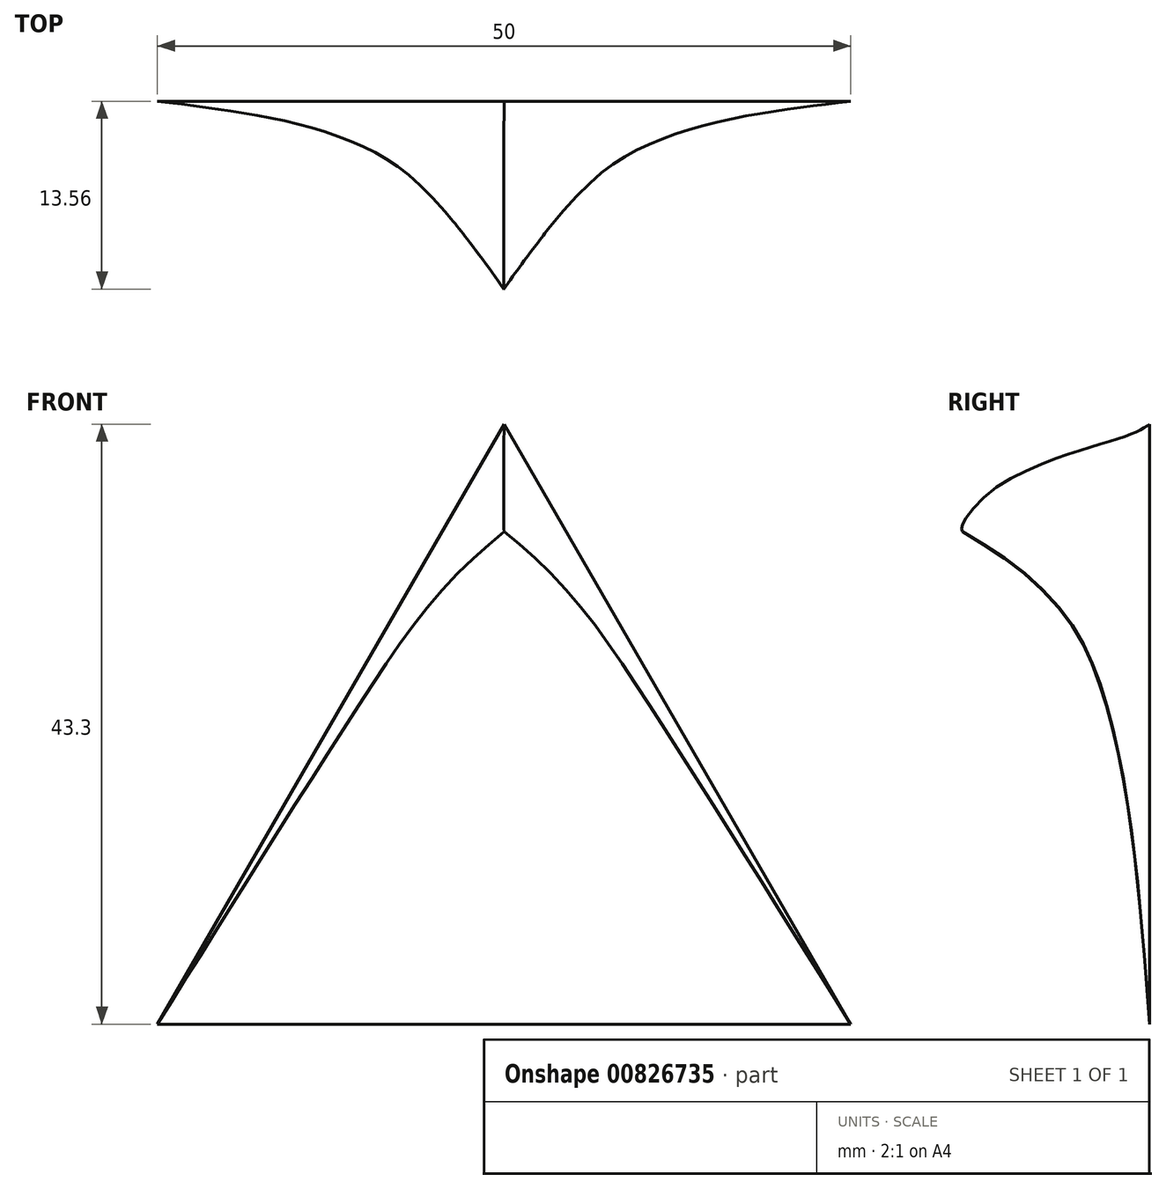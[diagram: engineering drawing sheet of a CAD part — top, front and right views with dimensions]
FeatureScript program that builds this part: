
annotation { "Feature Type Name" : "Feature", "Feature Type Description" : "" }
export const myFeature = defineFeature(function(context is Context, id is Id, definition is map)
    precondition{}
    {
        {
            var Q0;
            Q0=qCreatedBy(makeId("Front.planeOp"),FACE);
            var sketch = newSketch(context, id + "F0", { "sketchPlane" : qUnion([Q0])});
            skLineSegment(sketch, "E0", {"start": v(0, 0) * mm, "end": v(-50, 0) * mm});
            skLineSegment(sketch, "E1", {"start": v(-50, 0) * mm, "end": v(-25, 43.3) * mm});
            skLineSegment(sketch, "E2", {"start": v(0, 0) * mm, "end": v(-25, 43.3) * mm});
            skLineSegment(sketch, "E3", {"start": v(-25, 0) * mm, "end": v(-25, 43.3) * mm, "construction": true});
            skSolve(sketch);
        }
        {
            var Q0;
            Q0=sQuery(id+"F0.wireOp",EDGE,"E3");
            cPlane(context, id + "F1", {"entities" : qUnion([Q0]), "cplaneType" : CPlaneType.LINE_ANGLE, "offset" : 25 * mm, "angle" : 0 * degree, "width" : 150 * mm, "height" : 150 * mm});
        }
        {
            var Q0;
            Q0=qCreatedBy(id+"F1.planeOp",FACE);
            var sketch = newSketch(context, id + "F2", { "sketchPlane" : qUnion([Q0])});
            skPoint(sketch, "E4", {"position": v(-13.5, 35.54) * mm});
            skFitSpline(sketch, "E5", {"points": [v(0, 0) * mm, v(-5.05, 27.87) * mm, v(-13.5, 35.54) * mm], "startDerivative": vector(-4.13, 53.45) * mm, "endDerivative": vector(-24.38, 14.75) * mm});
            skSolve(sketch);
        }
        {
            var Q0;
            Q0=sQuery(id+"F2.wireOp",EDGE,"E5");
            var Q1;
            Q1=makeQuery(id+"F0.imprint","IMPRINT",FACE,{"disambiguationData":[TD([[makeQuery(id+"F0.imprint","IMPRINT",EDGE,{"derivedFrom":sQuery(id+"F0.wireOp",EDGE,"E0")}),-1.0]])]});
            var Q2;
            Q2=sQuery(id+"F2.wireOp",VERTEX,"E4");
            loft(context, id + "F3", {"addSections" : true, "spine" : qUnion([Q0]), "sectionCount" : 5, "sheetProfilesArray" : [{ "sheetProfileEntities" : qUnion([Q1]) }, { "sheetProfileEntities" : qUnion([Q2]) }]});
        }
    });
